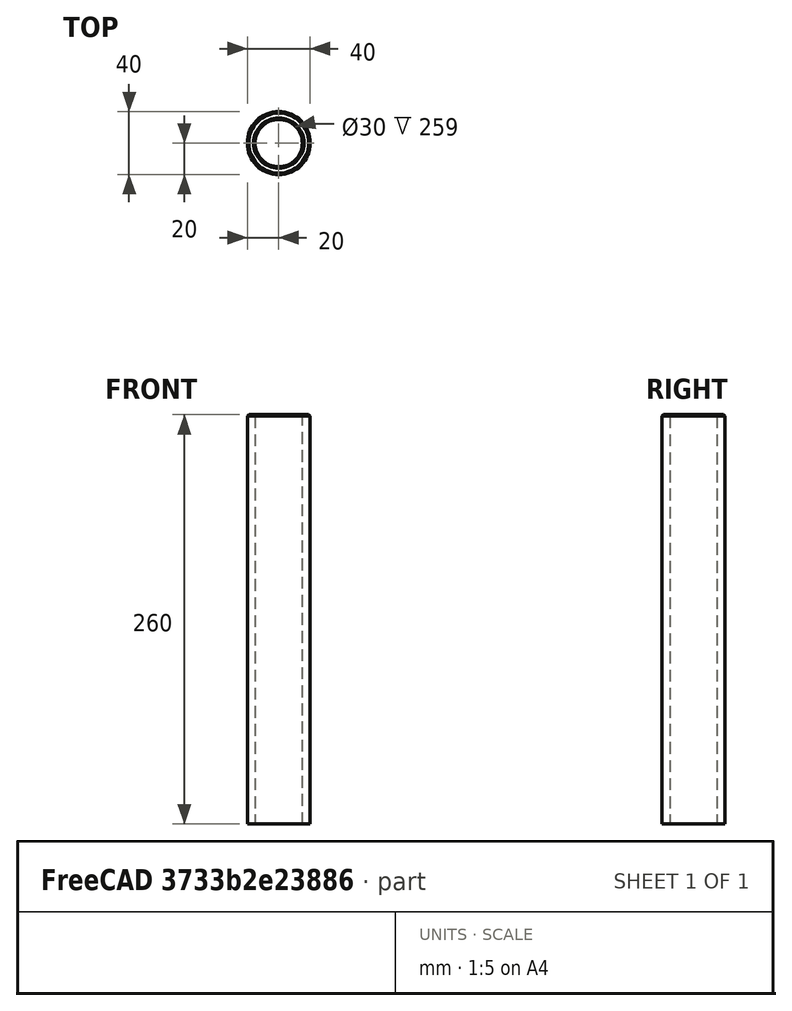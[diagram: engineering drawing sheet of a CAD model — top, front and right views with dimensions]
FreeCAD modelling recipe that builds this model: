
FCSTD DOCUMENT  (FreeCAD 1.0R39109 (Git))
Label: pipe
License: All rights reserved
LicenseURL: https://en.wikipedia.org/wiki/All_rights_reserved
objects: Sketcher::SketchObject×1, PartDesign::Pad×1, PartDesign::Chamfer×1, PartDesign::Body×1
note: 9 computed .brp shape members not serialized (recipe doc carries the construction recipe); baked Part::Feature solids carry a one-line shape summary decoded from their .brp

FEATURE [Sketcher::SketchObject] Sketch
  ArcFitTolerance = 1e-06
  AttachmentSupport = -> [XY_Plane]
  FullyConstrained = true
  MakeInternals = false
  MapMode = 5
  sketch-geometry (2):
    g0: Circle CenterX=0 CenterY=0 CenterZ=0 NormalX=0 NormalY=0 NormalZ=1 AngleXU=0 Radius=15
    g1: Circle CenterX=0 CenterY=0 CenterZ=0 NormalX=0 NormalY=0 NormalZ=1 AngleXU=0 Radius=20
  constraints (4):
    c: Diameter(g0) = 30
    c: Coincident(g0,g-1)
    c: Diameter(g1) = 40
    c: Coincident(g1,g0)
FEATURE [PartDesign::Pad] Pad
  Direction = (0,0,1)
  Length = 260
  Length2 = 10
  Profile = -> Sketch
  ReferenceAxis = -> Sketch [N_Axis]
  Refine = true
  Suppressed = false
  Type = 0
FEATURE [PartDesign::Chamfer] Chamfer
  Angle = 45
  Base = -> Pad [Edge6,Edge3]
  BaseFeature = -> Pad
  ChamferType = 0
  FlipDirection = false
  Refine = true
  Size = 1
  Size2 = 1
  SupportTransform = false
  Suppressed = false
  UseAllEdges = false
FEATURE [PartDesign::Body] Body
  AllowCompound = false
  Group = -> [Sketch,Pad,Chamfer]
  Origin = -> Origin
  Tip = -> Chamfer
